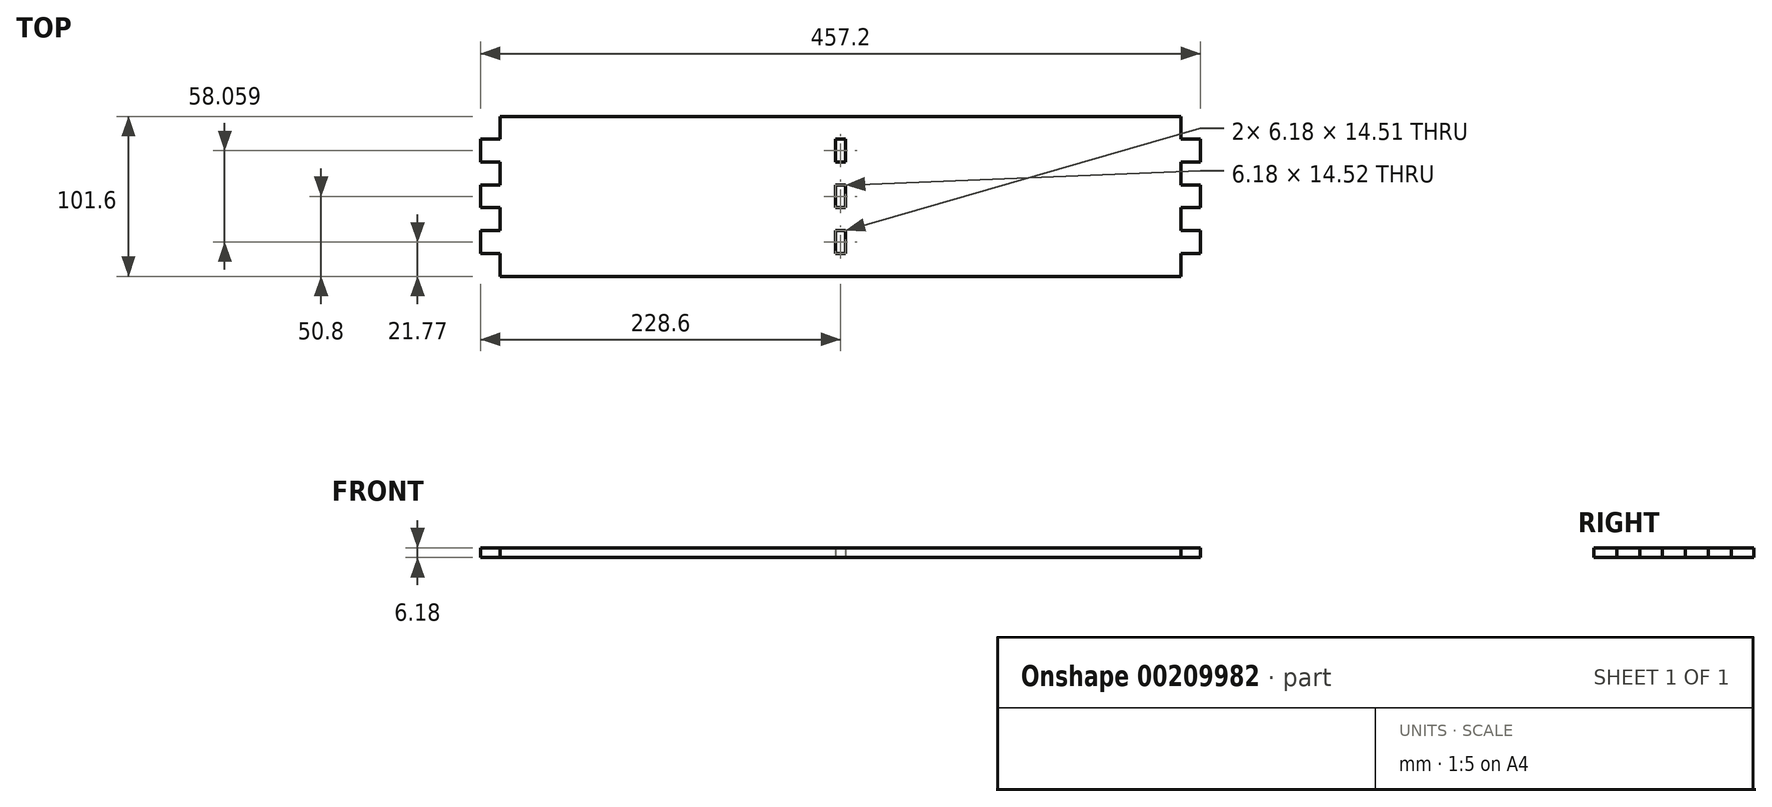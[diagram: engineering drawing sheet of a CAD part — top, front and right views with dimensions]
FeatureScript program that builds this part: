
annotation { "Feature Type Name" : "Feature", "Feature Type Description" : "" }
export const myFeature = defineFeature(function(context is Context, id is Id, definition is map)
    precondition{}
    {
        {
            var Q0;
            Q0=qCreatedBy(makeId("Top.planeOp"),FACE);
            var sketch = newSketch(context, id + "F0", { "sketchPlane" : qUnion([Q0])});
            skLineSegment(sketch, "E0.bottom", {"start": v(216.23, -50.8) * mm, "end": v(-216.23, -50.8) * mm});
            skLineSegment(sketch, "E0.top", {"start": v(216.23, 50.8) * mm, "end": v(-216.23, 50.8) * mm});
            skPoint(sketch, "E1.endSnap0", {"position": v(228.6, 0) * mm});
            skLineSegment(sketch, "E2", {"start": v(222.42, 36.29) * mm, "end": v(216.23, 36.29) * mm});
            skLineSegment(sketch, "E3", {"start": v(216.23, 21.77) * mm, "end": v(228.6, 21.77) * mm});
            skLineSegment(sketch, "E4", {"start": v(222.42, 7.26) * mm, "end": v(216.23, 7.26) * mm});
            skLineSegment(sketch, "E5.MirrorCS", {"start": v(222.42, -7.26) * mm, "end": v(216.23, -7.26) * mm});
            skLineSegment(sketch, "E6.MirrorCS", {"start": v(216.23, -21.77) * mm, "end": v(222.42, -21.77) * mm});
            skLineSegment(sketch, "E7.MirrorCS", {"start": v(222.42, -36.29) * mm, "end": v(216.23, -36.29) * mm});
            skPoint(sketch, "E8.MirrorCS.start.orphan", {"position": v(228.6, 50.8) * mm});
            skPoint(sketch, "E1.end.orphan", {"position": v(195.85, 0) * mm});
            skLineSegment(sketch, "E9.MirrorCS", {"start": v(-222.42, -7.26) * mm, "end": v(-216.23, -7.26) * mm});
            skLineSegment(sketch, "E10.MirrorCS", {"start": v(-222.42, 7.26) * mm, "end": v(-216.23, 7.26) * mm});
            skLineSegment(sketch, "E11.MirrorCS", {"start": v(-216.23, -21.77) * mm, "end": v(-222.42, -21.77) * mm});
            skLineSegment(sketch, "E12.MirrorCS", {"start": v(-216.23, 21.77) * mm, "end": v(-228.6, 21.77) * mm});
            skLineSegment(sketch, "E13.MirrorCS", {"start": v(-222.42, 36.29) * mm, "end": v(-216.23, 36.29) * mm});
            skPoint(sketch, "E14.MirrorP", {"position": v(-228.6, 0) * mm});
            skLineSegment(sketch, "E15.MirrorCS", {"start": v(-222.42, -36.29) * mm, "end": v(-216.23, -36.29) * mm});
            skPoint(sketch, "E16.MirrorP", {"position": v(-228.6, 50.8) * mm});
            skPoint(sketch, "E17.MirrorP", {"position": v(-195.85, 0) * mm});
            skPoint(sketch, "E18.MirrorCS.end.orphan", {"position": v(-222.42, 50.8) * mm});
            skLineSegment(sketch, "E19", {"start": v(222.42, 36.29) * mm, "end": v(228.6, 21.77) * mm});
            skLineSegment(sketch, "E20", {"start": v(222.42, 7.26) * mm, "end": v(222.42, -7.26) * mm});
            skLineSegment(sketch, "E21", {"start": v(222.42, -21.77) * mm, "end": v(222.42, -36.29) * mm});
            skLineSegment(sketch, "E22", {"start": v(-228.6, 36.29) * mm, "end": v(-228.6, 21.77) * mm});
            skLineSegment(sketch, "E23", {"start": v(-222.42, 7.26) * mm, "end": v(-222.42, -7.26) * mm});
            skLineSegment(sketch, "E24", {"start": v(-222.42, -21.77) * mm, "end": v(-222.42, -36.29) * mm});
            skLineSegment(sketch, "E25", {"start": v(-216.23, 36.29) * mm, "end": v(-216.23, 50.8) * mm});
            skLineSegment(sketch, "E26", {"start": v(-216.23, 21.77) * mm, "end": v(-216.23, 7.26) * mm});
            skLineSegment(sketch, "E27", {"start": v(-216.23, -7.26) * mm, "end": v(-216.23, -21.77) * mm});
            skLineSegment(sketch, "E28", {"start": v(-216.23, -36.29) * mm, "end": v(-216.23, -50.8) * mm});
            skPoint(sketch, "E29.MirrorCS.start.orphan", {"position": v(-222.42, -50.8) * mm});
            skPoint(sketch, "E30.MirrorCS.end.orphan", {"position": v(-222.42, 0) * mm});
            skLineSegment(sketch, "E31", {"start": v(216.23, 36.29) * mm, "end": v(216.23, 50.8) * mm});
            skLineSegment(sketch, "E32", {"start": v(216.23, 21.77) * mm, "end": v(216.23, 7.26) * mm});
            skLineSegment(sketch, "E33", {"start": v(216.23, -7.26) * mm, "end": v(216.23, -21.77) * mm});
            skLineSegment(sketch, "E34", {"start": v(216.23, -36.29) * mm, "end": v(216.23, -50.8) * mm});
            skPoint(sketch, "E35.trimOffspring.end.orphan", {"position": v(222.42, 50.8) * mm});
            skPoint(sketch, "E36.MirrorCS.end.orphan", {"position": v(222.42, 0) * mm});
            skPoint(sketch, "E37.orphan", {"position": v(222.42, -50.8) * mm});
            skPoint(sketch, "E38.orphan", {"position": v(234.78, -50.8) * mm});
            skPoint(sketch, "E39.MirrorP", {"position": v(3.1, 0) * mm});
            skLineSegment(sketch, "E40.MirrorCS", {"start": v(-3.1, -21.77) * mm, "end": v(3.1, -21.77) * mm});
            skLineSegment(sketch, "E41.MirrorCS", {"start": v(-3.1, 21.77) * mm, "end": v(3.1, 21.77) * mm});
            skLineSegment(sketch, "E42.MirrorCS", {"start": v(3.1, 7.26) * mm, "end": v(-3.1, 7.26) * mm});
            skLineSegment(sketch, "E43.MirrorCS", {"start": v(3.1, -7.26) * mm, "end": v(-3.1, -7.26) * mm});
            skLineSegment(sketch, "E44.MirrorCS", {"start": v(3.1, 7.26) * mm, "end": v(3.1, -7.26) * mm});
            skLineSegment(sketch, "E45.MirrorCS", {"start": v(3.1, 36.29) * mm, "end": v(-3.1, 36.29) * mm});
            skPoint(sketch, "E46.MirrorP", {"position": v(3.1, 50.8) * mm});
            skLineSegment(sketch, "E47.MirrorCS", {"start": v(3.1, -36.29) * mm, "end": v(-3.1, -36.29) * mm});
            skLineSegment(sketch, "E48.MirrorCS", {"start": v(-447.92, -50.8) * mm, "end": v(-3.1, -50.8) * mm});
            skPoint(sketch, "E49.MirrorP", {"position": v(3.1, -50.8) * mm});
            skPoint(sketch, "E50.MirrorP", {"position": v(-3.1, 0) * mm});
            skLineSegment(sketch, "E51.MirrorCS", {"start": v(3.1, -21.77) * mm, "end": v(3.1, -36.29) * mm});
            skLineSegment(sketch, "E52.MirrorCS", {"start": v(3.1, 36.29) * mm, "end": v(3.1, 21.77) * mm});
            skLineSegment(sketch, "E53.MirrorCS", {"start": v(-447.92, 50.8) * mm, "end": v(-3.1, 50.8) * mm});
            skLineSegment(sketch, "E54", {"start": v(-3.1, 36.29) * mm, "end": v(-3.1, 21.77) * mm});
            skLineSegment(sketch, "E55", {"start": v(-3.1, 7.26) * mm, "end": v(-3.1, -7.26) * mm});
            skLineSegment(sketch, "E56", {"start": v(-3.1, -21.77) * mm, "end": v(-3.1, -36.29) * mm});
            skLineSegment(sketch, "E57", {"start": v(-228.6, 36.29) * mm, "end": v(-222.42, 36.29) * mm});
            skLineSegment(sketch, "E58", {"start": v(-222.42, 7.26) * mm, "end": v(-228.6, 7.26) * mm});
            skLineSegment(sketch, "E59", {"start": v(-228.6, 7.26) * mm, "end": v(-228.6, -7.26) * mm});
            skLineSegment(sketch, "E60", {"start": v(-228.6, -7.26) * mm, "end": v(-222.42, -7.26) * mm});
            skLineSegment(sketch, "E61", {"start": v(-222.42, -21.77) * mm, "end": v(-228.6, -21.77) * mm});
            skLineSegment(sketch, "E62", {"start": v(-222.42, -36.29) * mm, "end": v(-228.6, -36.29) * mm});
            skLineSegment(sketch, "E63", {"start": v(-228.6, -36.29) * mm, "end": v(-228.6, -21.77) * mm});
            skLineSegment(sketch, "E64", {"start": v(222.42, 36.29) * mm, "end": v(228.6, 36.29) * mm});
            skLineSegment(sketch, "E65", {"start": v(228.6, 36.29) * mm, "end": v(228.6, 21.77) * mm});
            skLineSegment(sketch, "E66", {"start": v(222.42, 7.26) * mm, "end": v(228.6, 7.26) * mm});
            skLineSegment(sketch, "E67", {"start": v(222.42, -7.26) * mm, "end": v(228.6, -7.26) * mm});
            skLineSegment(sketch, "E68", {"start": v(228.6, -7.26) * mm, "end": v(228.6, 7.26) * mm});
            skLineSegment(sketch, "E69", {"start": v(222.42, -21.77) * mm, "end": v(228.6, -21.77) * mm});
            skLineSegment(sketch, "E70", {"start": v(222.42, -36.29) * mm, "end": v(228.6, -36.29) * mm});
            skLineSegment(sketch, "E71", {"start": v(228.6, -36.29) * mm, "end": v(228.6, -21.77) * mm});
            skSolve(sketch);
        }
        {
            var Q0;
            Q0 = qSketchRegion(id + "F0", true);
            extrude(context, id + "F1", {"entities" : qUnion([Q0]), "depth" : 6.18 * mm});
        }
    });
